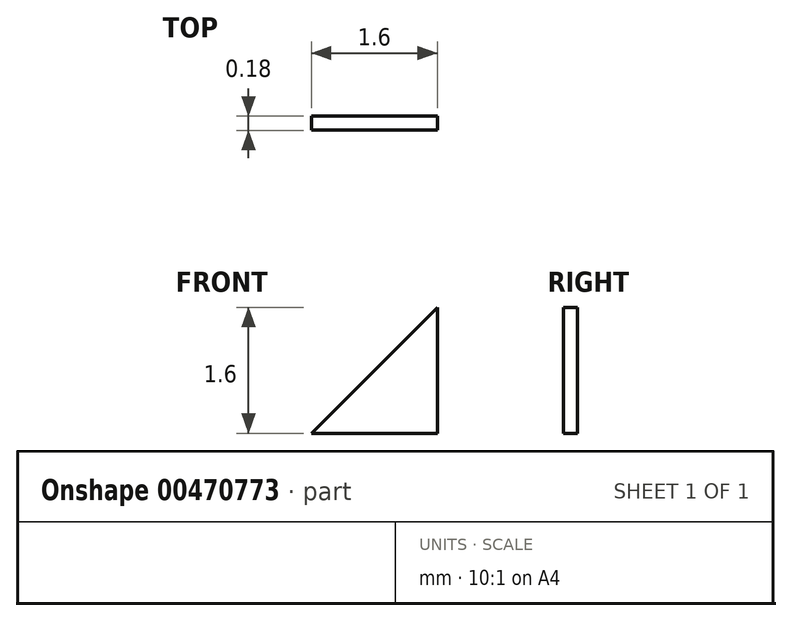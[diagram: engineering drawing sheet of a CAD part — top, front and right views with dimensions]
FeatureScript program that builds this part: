
annotation { "Feature Type Name" : "Feature", "Feature Type Description" : "" }
export const myFeature = defineFeature(function(context is Context, id is Id, definition is map)
    precondition{}
    {
        {
            var Q0;
            Q0=qCreatedBy(makeId("Front.planeOp"),FACE);
            var sketch = newSketch(context, id + "F0", { "sketchPlane" : qUnion([Q0])});
            skLineSegment(sketch, "E0", {"start": v(0, 1.6) * mm, "end": v(0, 0) * mm});
            skLineSegment(sketch, "E1", {"start": v(0, 0) * mm, "end": v(-1.6, 0) * mm});
            skLineSegment(sketch, "E2", {"start": v(-1.6, 0) * mm, "end": v(0, 1.6) * mm});
            skSolve(sketch);
        }
        {
            var Q0;
            Q0=makeQuery(id+"F0.imprint","IMPRINT",FACE,{"disambiguationData":[TD([[makeQuery(id+"F0.imprint","IMPRINT",EDGE,{"derivedFrom":sQuery(id+"F0.wireOp",EDGE,"E0")}),-1.0]])]});
            extrude(context, id + "F1", {"entities" : qUnion([Q0]), "depth" : 0.18 * mm});
        }
    });
